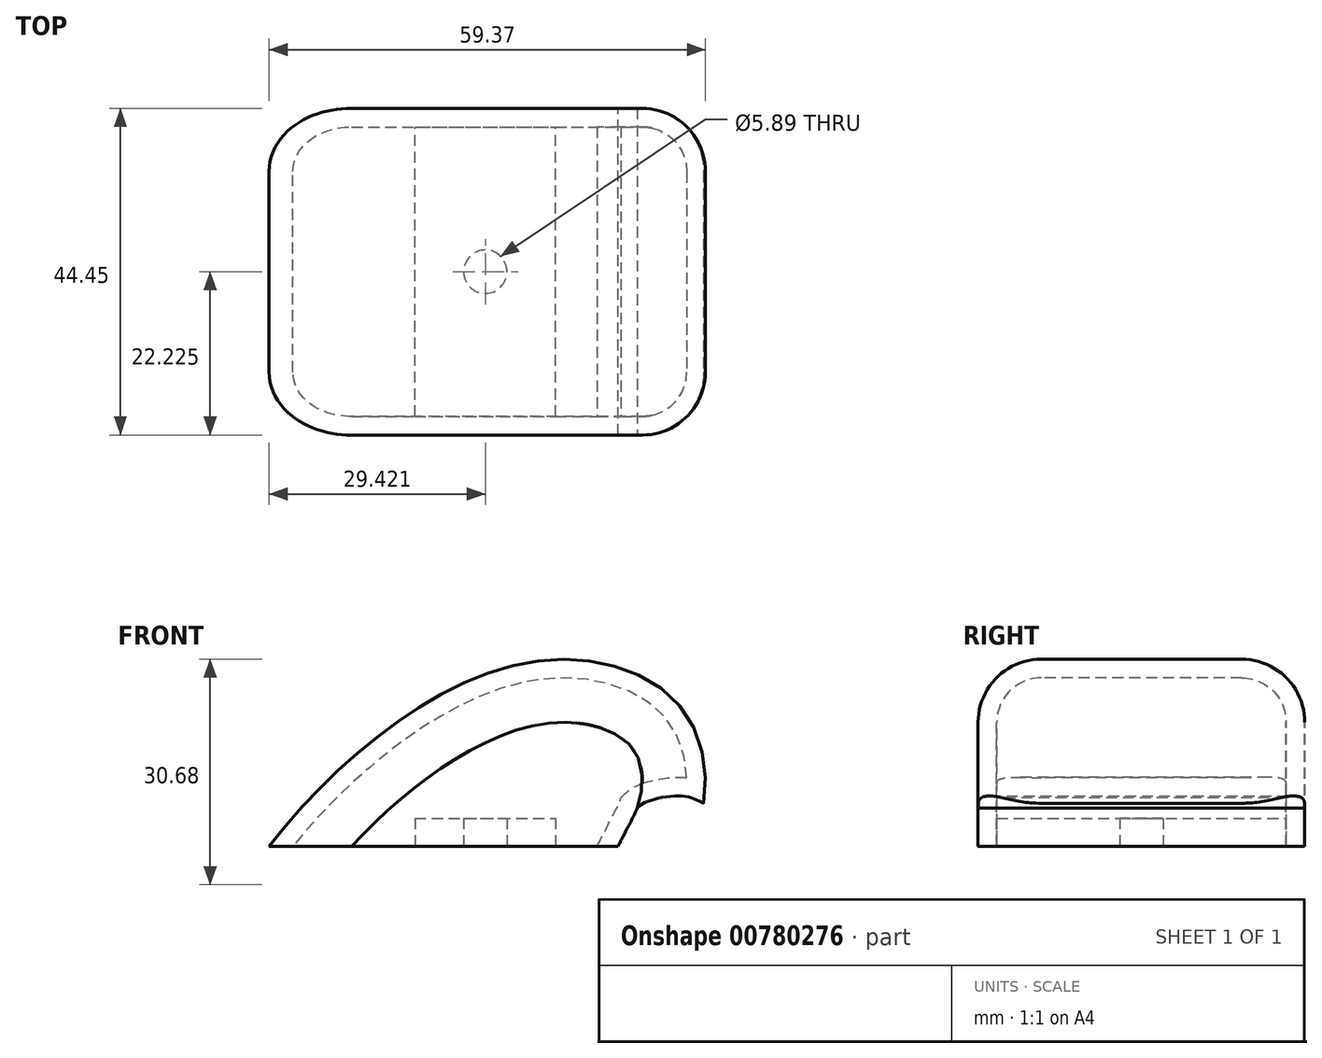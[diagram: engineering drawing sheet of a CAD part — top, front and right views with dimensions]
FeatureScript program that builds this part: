
annotation { "Feature Type Name" : "Feature", "Feature Type Description" : "" }
export const myFeature = defineFeature(function(context is Context, id is Id, definition is map)
    precondition{}
    {
        {
            var Q0;
            Q0=qCreatedBy(makeId("Front.planeOp"),FACE);
            var sketch = newSketch(context, id + "F0", { "sketchPlane" : qUnion([Q0])});
            skLineSegment(sketch, "E0", {"start": v(-73.44, 12.37) * mm, "end": v(-16.3, 12.37) * mm});
            skFitSpline(sketch, "E1", {"points": [v(-73.44, 12.37) * mm, v(-51.46, 32.22) * mm, v(-31.91, 37.77) * mm, v(-16.95, 30.7) * mm, v(-16.3, 12.37) * mm], "startDerivative": vector(61.6, 80.1) * mm, "endDerivative": vector(-42.51, -82.23) * mm});
            skSolve(sketch);
        }
        {
            var Q0;
            Q0=makeQuery(id+"F0.imprint","IMPRINT",FACE,{"disambiguationData":[TD([[makeQuery(id+"F0.imprint","IMPRINT",EDGE,{"derivedFrom":sQuery(id+"F0.wireOp",EDGE,"E0")}),1.0]])]});
            extrude(context, id + "F1", {"entities" : qUnion([Q0]), "depth" : 44.45 * mm, "offsetDistance" : 25.4 * mm});
        }
        {
            var Q0;
            Q0=makeQuery(id+"F1.opExtrude","CAP_EDGE",EDGE,{"disambiguationData":[OSD([sQuery(id+"F0.wireOp",EDGE,"E1")])],"isStart":false});
            var Q1;
            Q1=makeQuery(id+"F1.opExtrude","CAP_EDGE",EDGE,{"disambiguationData":[OSD([sQuery(id+"F0.wireOp",EDGE,"E1")])],"isStart":true});
            fillet(context, id + "F2", {"entities" : qUnion([Q0, Q1]), "radius" : 8.58 * mm, "tangentPropagation" : true, "allowEdgeOverflow" : false});
        }
        {
            var Q0;
            Q0=makeQuery(id+"F1.opExtrude","CAP_FACE",FACE,{"disambiguationData":[OSD([sQuery(id+"F0.wireOp",EDGE,"E0"),sQuery(id+"F0.wireOp",EDGE,"E1")])],"isStart":false});
            var sketch = newSketch(context, id + "F3", { "sketchPlane" : qUnion([Q0])});
            skLineSegment(sketch, "E2", {"start": v(-25.96, 12.37) * mm, "end": v(-7.69, 12.37) * mm});
            skLineSegment(sketch, "E3", {"start": v(-7.69, 12.37) * mm, "end": v(-13.2, 17.6) * mm});
            skFitSpline(sketch, "E4", {"points": [v(-13.2, 17.6) * mm, v(-16.57, 19.1) * mm, v(-19.86, 19.01) * mm, v(-23.35, 17.6) * mm, v(-25.96, 12.37) * mm], "startDerivative": vector(-14.17, 8) * mm, "endDerivative": vector(-7.03, -20.6) * mm});
            skSolve(sketch);
        }
        {
            var Q0;
            {var subQ0=sQuery(id+"F3.wireOp",EDGE,"E2");Q0=makeQuery(id+"F3.imprint","IMPRINT",FACE,{"disambiguationData":[TD([[makeQuery(id+"F3.imprint","IMPRINT",EDGE,{"derivedFrom":subQ0}),1.0]])]});}
            extrude(context, id + "F4", {"entities" : qUnion([Q0]), "operationType" : NewBodyOperationType.REMOVE, "oppositeDirection" : true, "depth" : 48.5 * mm, "offsetDistance" : 25.4 * mm});
        }
        {
            var Q0;
            Q0=makeQuery(id+"F1.opExtrude","SWEPT_FACE",FACE,{"disambiguationData":[OSD([sQuery(id+"F0.wireOp",EDGE,"E0")])]});
            shell(context, id + "F5", {"entities" : qUnion([Q0]), "thickness" : 2.54 * mm});
        }
        {
            var Q0;
            Q0=makeQuery(id+"F1.opExtrude","SWEPT_FACE",FACE,{"disambiguationData":[OSD([sQuery(id+"F0.wireOp",EDGE,"E0")])]});
            var sketch = newSketch(context, id + "F6", { "sketchPlane" : qUnion([Q0])});
            skLineSegment(sketch, "E5.bottom", {"start": v(-53.6, 44.45) * mm, "end": v(-34.45, 44.45) * mm});
            skLineSegment(sketch, "E5.top", {"start": v(-53.6, 0) * mm, "end": v(-34.45, 0) * mm});
            skLineSegment(sketch, "E5.left", {"start": v(-53.6, 44.45) * mm, "end": v(-53.6, 0) * mm});
            skLineSegment(sketch, "E5.right", {"start": v(-34.45, 44.45) * mm, "end": v(-34.45, 0) * mm});
            skCircle(sketch, "E6", {"center": v(-44.02, 22.23) * mm, "radius": 2.95 * mm});
            skPoint(sketch, "E6.centerSnap0", {"position": v(-34.45, 22.23) * mm});
            skPoint(sketch, "E6.centerSnap1", {"position": v(-44.02, 44.45) * mm});
            skSolve(sketch);
        }
        {
            var Q0;
            Q0 = qSketchRegion(id + "F6", true);
            extrude(context, id + "F7", {"entities" : qUnion([Q0]), "operationType" : NewBodyOperationType.ADD, "oppositeDirection" : true, "depth" : 3.8 * mm, "offsetDistance" : 25.4 * mm});
        }
    });
